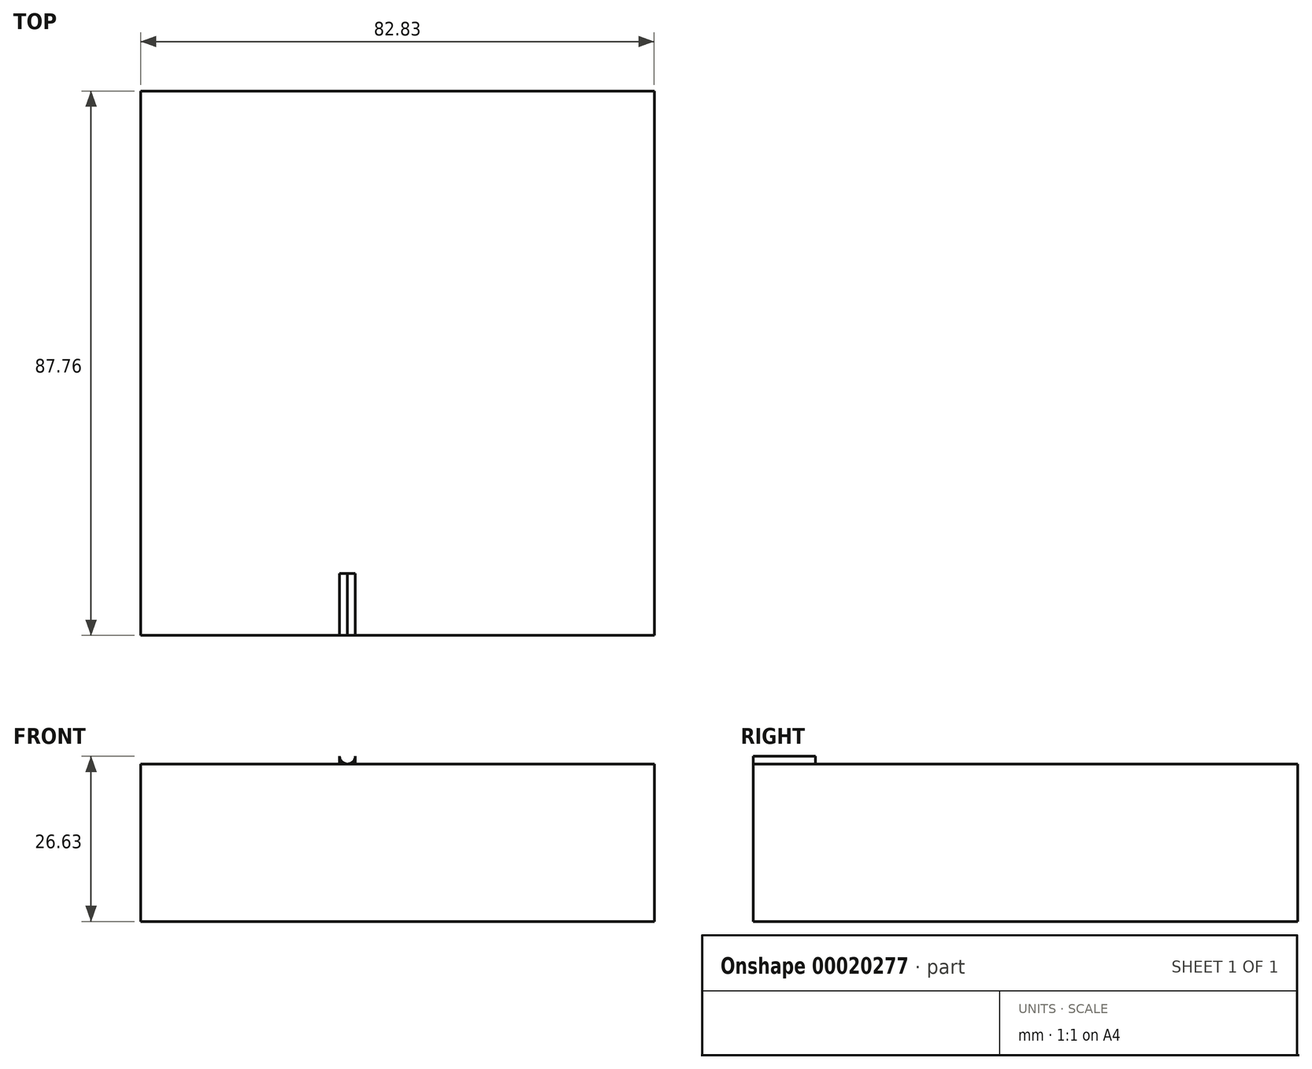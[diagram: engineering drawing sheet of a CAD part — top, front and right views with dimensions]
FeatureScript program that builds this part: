
annotation { "Feature Type Name" : "Feature", "Feature Type Description" : "" }
export const myFeature = defineFeature(function(context is Context, id is Id, definition is map)
    precondition{}
    {
        {
            var Q0;
            Q0=qCreatedBy(makeId("Top.planeOp"),FACE);
            var sketch = newSketch(context, id + "F0", { "sketchPlane" : qUnion([Q0])});
            skLineSegment(sketch, "E0.bottom", {"start": v(-45.43, 48.75) * mm, "end": v(37.4, 48.75) * mm});
            skLineSegment(sketch, "E0.top", {"start": v(-45.43, -39) * mm, "end": v(37.4, -39) * mm});
            skLineSegment(sketch, "E0.left", {"start": v(-45.43, 48.75) * mm, "end": v(-45.43, -39) * mm});
            skLineSegment(sketch, "E0.right", {"start": v(37.4, 48.75) * mm, "end": v(37.4, -39) * mm});
            skSolve(sketch);
        }
        {
            var Q0;
            Q0=makeQuery(id+"F0.imprint","IMPRINT",FACE,{"disambiguationData":[TD([[makeQuery(id+"F0.imprint","IMPRINT",EDGE,{"derivedFrom":sQuery(id+"F0.wireOp",EDGE,"E0.bottom")}),-1.0]])]});
            extrude(context, id + "F1", {"entities" : qUnion([Q0]), "depth" : 25.4 * mm});
        }
        {
            var Q0;
            Q0=makeQuery(id+"F1.opExtrude","SWEPT_FACE",FACE,{"disambiguationData":[OSD([sQuery(id+"F0.wireOp",EDGE,"E0.top")])]});
            var sketch = newSketch(context, id + "F2", { "sketchPlane" : qUnion([Q0])});
            skCircle(sketch, "E1", {"center": v(-12.08, 26.67) * mm, "radius": 1.27 * mm});
            skLineSegment(sketch, "E2.bottom", {"start": v(-13.35, 25.4) * mm, "end": v(-10.81, 25.4) * mm});
            skLineSegment(sketch, "E2.top", {"start": v(-13.35, 26.63) * mm, "end": v(-10.81, 26.63) * mm});
            skLineSegment(sketch, "E2.left", {"start": v(-13.35, 25.4) * mm, "end": v(-13.35, 26.63) * mm});
            skLineSegment(sketch, "E2.right", {"start": v(-10.81, 25.4) * mm, "end": v(-10.81, 26.63) * mm});
            skSolve(sketch);
        }
        {
            var Q0;
            {var subQ0=sQuery(id+"F2.wireOp",EDGE,"E2.right");Q0=makeQuery(id+"F2.imprint","IMPRINT",FACE,{"disambiguationData":[TD([[makeQuery(id+"F2.imprint","IMPRINT",EDGE,{"derivedFrom":subQ0}),1.0]])]});}
            extrude(context, id + "F3", {"entities" : qUnion([Q0]), "oppositeDirection" : true, "depth" : 10 * mm});
        }
        {
            var Q0;
            {var subQ0=sQuery(id+"F2.wireOp",EDGE,"E2.left");Q0=makeQuery(id+"F2.imprint","IMPRINT",FACE,{"disambiguationData":[TD([[makeQuery(id+"F2.imprint","IMPRINT",EDGE,{"derivedFrom":subQ0}),-1.0]])]});}
            extrude(context, id + "F4", {"entities" : qUnion([Q0]), "oppositeDirection" : true, "depth" : 10 * mm});
        }
    });
